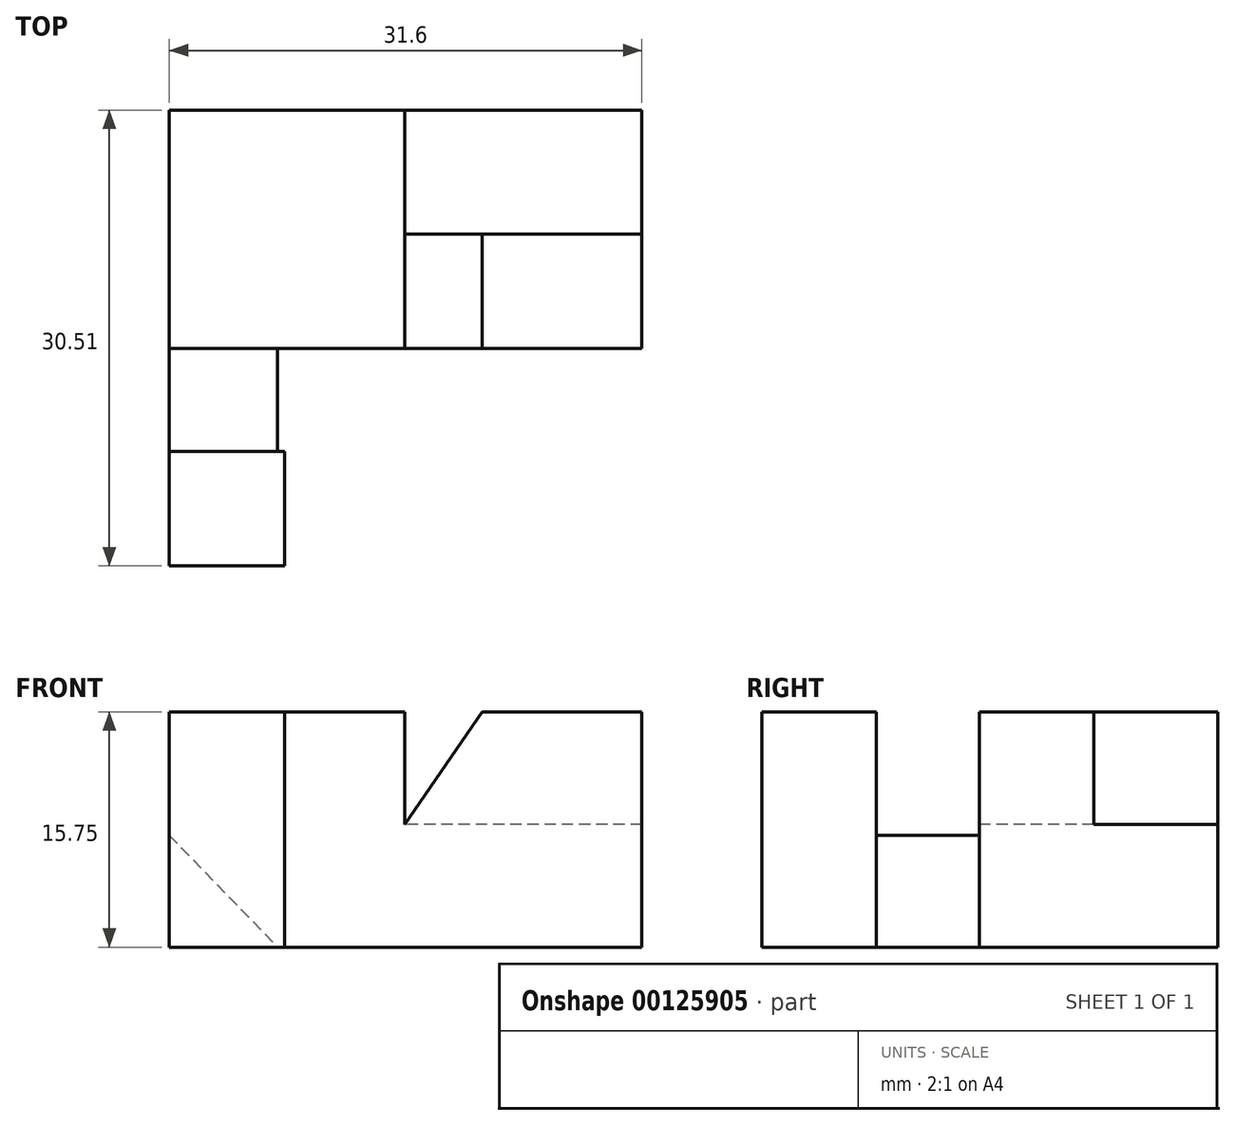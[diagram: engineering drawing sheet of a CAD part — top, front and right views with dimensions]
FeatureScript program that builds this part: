
annotation { "Feature Type Name" : "Feature", "Feature Type Description" : "" }
export const myFeature = defineFeature(function(context is Context, id is Id, definition is map)
    precondition{}
    {
        {
            var Q0;
            Q0=qCreatedBy(makeId("Front.planeOp"),FACE);
            var sketch = newSketch(context, id + "F0", { "sketchPlane" : qUnion([Q0])});
            skLineSegment(sketch, "E0.bottom", {"start": v(0, 0) * mm, "end": v(15.75, 0) * mm});
            skLineSegment(sketch, "E0.top", {"start": v(0, 15.75) * mm, "end": v(15.75, 15.75) * mm});
            skLineSegment(sketch, "E0.left", {"start": v(0, 0) * mm, "end": v(0, 15.75) * mm});
            skLineSegment(sketch, "E0.right", {"start": v(15.75, 0) * mm, "end": v(15.75, 15.75) * mm});
            skSolve(sketch);
        }
        {
            var Q0;
            Q0=makeQuery(id+"F0.imprint","IMPRINT",FACE,{"disambiguationData":[TD([[makeQuery(id+"F0.imprint","IMPRINT",EDGE,{"derivedFrom":sQuery(id+"F0.wireOp",EDGE,"E0.bottom")}),1.0]])]});
            extrude(context, id + "F1", {"entities" : qUnion([Q0]), "depth" : 15.95 * mm});
        }
        {
            var Q0;
            Q0=makeQuery(id+"F1.opExtrude","CAP_FACE",FACE,{"disambiguationData":[OSD([sQuery(id+"F0.wireOp",EDGE,"E0.bottom"),sQuery(id+"F0.wireOp",EDGE,"E0.top"),sQuery(id+"F0.wireOp",EDGE,"E0.left"),sQuery(id+"F0.wireOp",EDGE,"E0.right")])],"isStart":false});
            var sketch = newSketch(context, id + "F2", { "sketchPlane" : qUnion([Q0])});
            skLineSegment(sketch, "E1", {"start": v(0, 0) * mm, "end": v(7.24, 0) * mm});
            skLineSegment(sketch, "E2", {"start": v(0, 0) * mm, "end": v(0, 7.47) * mm});
            skLineSegment(sketch, "E3", {"start": v(0, 7.47) * mm, "end": v(7.24, 0) * mm});
            skSolve(sketch);
        }
        {
            var Q0;
            Q0=makeQuery(id+"F2.imprint","IMPRINT",FACE,{"disambiguationData":[TD([[makeQuery(id+"F2.imprint","IMPRINT",EDGE,{"derivedFrom":sQuery(id+"F2.wireOp",EDGE,"E1")}),1.0]])]});
            extrude(context, id + "F3", {"entities" : qUnion([Q0]), "operationType" : NewBodyOperationType.ADD, "depth" : 6.88 * mm});
        }
        {
            var Q0;
            Q0=makeQuery(id+"F3.opExtrude","CAP_FACE",FACE,{"disambiguationData":[OSD([sQuery(id+"F2.wireOp",EDGE,"E1"),sQuery(id+"F2.wireOp",EDGE,"E2"),sQuery(id+"F2.wireOp",EDGE,"E3")])],"isStart":false});
            var sketch = newSketch(context, id + "F4", { "sketchPlane" : qUnion([Q0])});
            skLineSegment(sketch, "E4", {"start": v(0, 0) * mm, "end": v(7.7, 0) * mm});
            skLineSegment(sketch, "E5", {"start": v(7.7, 0) * mm, "end": v(7.7, 15.75) * mm});
            skLineSegment(sketch, "E6", {"start": v(0, 15.75) * mm, "end": v(0, 0) * mm});
            skLineSegment(sketch, "E7.0", {"start": v(0, 15.75) * mm, "end": v(7.7, 15.75) * mm});
            skPoint(sketch, "E8.end.orphan", {"position": v(0, 16.05) * mm});
            skPoint(sketch, "E9.orphan", {"position": v(7.7, 16.05) * mm});
            skPoint(sketch, "E10.orphan", {"position": v(15.75, 15.75) * mm});
            skSolve(sketch);
        }
        {
            var Q0;
            {var subQ4=sQuery(id+"F4.wireOp",EDGE,"E5");Q0=makeQuery(id+"F4.imprint","IMPRINT",FACE,{"disambiguationData":[TD([[makeQuery(id+"F4.imprint","IMPRINT",EDGE,{"derivedFrom":subQ4}),1.0]])]});}
            var Q1;
            {var subQ3=makeQuery(id+"F3.opExtrude","CAP_EDGE",EDGE,{"disambiguationData":[OSD([sQuery(id+"F2.wireOp",EDGE,"E3")])],"isStart":false});Q1=makeQuery(id+"F4.imprint","IMPRINT",FACE,{"disambiguationData":[TD([[makeQuery(id+"F4.imprint","IMPRINT",EDGE,{"derivedFrom":subQ3}),-1.0]])]});}
            extrude(context, id + "F5", {"entities" : qUnion([Q0, Q1]), "operationType" : NewBodyOperationType.ADD, "depth" : 7.67 * mm});
        }
        {
            var Q0;
            Q0=makeQuery(id+"F1.opExtrude","SWEPT_FACE",FACE,{"disambiguationData":[OSD([sQuery(id+"F0.wireOp",EDGE,"E0.right")])]});
            var sketch = newSketch(context, id + "F6", { "sketchPlane" : qUnion([Q0])});
            skLineSegment(sketch, "E11", {"start": v(0, 0) * mm, "end": v(0, 8.2) * mm});
            skLineSegment(sketch, "E12.bottom", {"start": v(0, 8.2) * mm, "end": v(-15.95, 8.2) * mm});
            skLineSegment(sketch, "E12.top", {"start": v(0, 0) * mm, "end": v(-15.95, 0) * mm});
            skLineSegment(sketch, "E12.left", {"start": v(0, 8.2) * mm, "end": v(0, 0) * mm});
            skLineSegment(sketch, "E12.right", {"start": v(-15.95, 8.2) * mm, "end": v(-15.95, 0) * mm});
            skSolve(sketch);
        }
        {
            var Q0;
            Q0=makeQuery(id+"F6.imprint","IMPRINT",FACE,{"disambiguationData":[TD([[makeQuery(id+"F6.imprint","IMPRINT",EDGE,{"derivedFrom":sQuery(id+"F6.wireOp",EDGE,"E12.bottom")}),1.0]])]});
            extrude(context, id + "F7", {"entities" : qUnion([Q0]), "operationType" : NewBodyOperationType.ADD, "depth" : 15.85 * mm});
        }
        {
            var Q0;
            Q0=makeQuery(id+"F7.boolean.opBoolean","MERGE",FACE,{"derivedFrom":[makeQuery(id+"F1.opExtrude","CAP_FACE",FACE,{"disambiguationData":[OSD([sQuery(id+"F0.wireOp",EDGE,"E0.bottom"),sQuery(id+"F0.wireOp",EDGE,"E0.top"),sQuery(id+"F0.wireOp",EDGE,"E0.left"),sQuery(id+"F0.wireOp",EDGE,"E0.right")])],"isStart":false}),makeQuery(id+"F7.opExtrude","SWEPT_FACE",FACE,{"disambiguationData":[OSD([sQuery(id+"F6.wireOp",EDGE,"E12.right")])]})]});
            var sketch = newSketch(context, id + "F8", { "sketchPlane" : qUnion([Q0])});
            skLineSegment(sketch, "E13", {"start": v(15.75, 8.2) * mm, "end": v(20.92, 15.75) * mm});
            skLineSegment(sketch, "E14", {"start": v(20.92, 15.75) * mm, "end": v(31.6, 15.75) * mm});
            skLineSegment(sketch, "E15", {"start": v(31.6, 15.75) * mm, "end": v(31.6, 8.2) * mm});
            skSolve(sketch);
        }
        {
            var Q0;
            Q0 = qSketchRegion(id + "F8", true);
            var Q1;
            Q1=makeQuery(id+"F8.imprint","IMPRINT",FACE,{"disambiguationData":[TD([[makeQuery(id+"F8.imprint","IMPRINT",EDGE,{"derivedFrom":sQuery(id+"F8.wireOp",EDGE,"E13")}),-1.0]])]});
            extrude(context, id + "F9", {"entities" : qUnion([Q0, Q1]), "operationType" : NewBodyOperationType.ADD, "oppositeDirection" : true, "depth" : 7.65 * mm});
        }
    });
